# Revit family: GE6 -4 Panels
name_source: partatom
category: Furniture
units: mm (PartAtom-declared; Revit-internal decimal feet)

## family parameters
Always vertical = Yes
Cut with Voids When Loaded = No
OmniClass Number = 23.40.20.00
OmniClass Title = General Furniture and Specialties
Room Calculation Point = No
Shared = No
Work Plane-Based = No

## types (2) — shared parameters
Assembly Code = E2020200
Base = Gresham - SILVER METAL
Depth = 300 mm  [stored 0.984252 ft]
Fins = GABRIEL Byron_15101
Manufacturer = Gresham Office Furniture
Model = GE6
Range = SCREENS
Supports = Gresham - SILVER METAL
URL = www.gof.co.uk

## per-type parameters (varying)
| type | Product Code | Support Dimensions | Width |
| 1000 x 300 x 1800 High | GE6C2 | 250 mm  [stored 0.82021 ft] | 1000 mm  [stored 3.28084 ft] |
| 1200 x 300 x 1800 High | GE6D2 | 300 mm  [stored 0.984252 ft] | 1200 mm |

note: [stored X ft] marks values corroborated as IEEE doubles in the binary element streams (Revit-internal decimal feet)

## geometry (parser evidence)
native form markers: Sweep x2
no freeform markers — native parametric forms only
